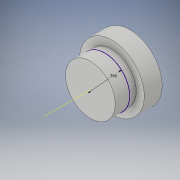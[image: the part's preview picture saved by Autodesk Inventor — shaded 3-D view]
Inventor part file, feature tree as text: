
AUTODESK INVENTOR PART (.ipt)
format: ipt  version: 2019 (Build 230136000, 136)  size: 112,640 bytes
history: native  units: in
note: dims shown in document units (in); Inventor stores cm internally (conversion verified against a paired STEP export)
features: extrude x3, sketch x3, other x1
ambient origin geometry x8: Origin, YZ Plane, XZ Plane, XY Plane, X Axis, Y Axis, Z Axis, Center Point
bodies: Solid1 (feature_tree)
feature tree (7):
  extrude  "Extrusion1"  Depth=0.125in TaperAngle=0.0deg
  extrude  "Extrusion2"  Depth=0.05in TaperAngle=0.0deg
  extrude  "Extrusion3"  Depth=0.1in TaperAngle=0.0deg
  other  "Work Axis1"
  sketch  "Sketch1"  dims[d0=0.45in d1=0.125in d2=0.0in]
  sketch  "Sketch2"  dims[d3=0.34in d4=0.05in d5=0.0in]
  sketch  "Sketch3"  dims[d6=0.345in d7=0.1in d8=0.0in]
